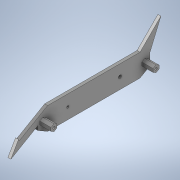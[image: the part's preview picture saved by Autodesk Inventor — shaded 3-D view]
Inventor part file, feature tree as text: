
AUTODESK INVENTOR PART (.ipt)
format: ipt  version: 2020 (Build 240168000, 168)  size: 182,272 bytes
history: native  units: in
note: dims shown in document units (in); Inventor stores cm internally (conversion verified against a paired STEP export)
features: other x3, extrude x2, sketch x2
ambient origin geometry x8: Origin, YZ Plane, XZ Plane, XY Plane, X Axis, Y Axis, Z Axis, Center Point
bodies: Solid1 (feature_tree)
feature tree (7):
  other  "HexWheelGuard.ipt"
  extrude  "Extrusion1"  TaperAngle=0.0deg  [1 undecoded]
  extrude  "Extrusion2"  Depth=0.5906in
  other  "Solid1::HexWheelGuard.ipt"
  other  "TaggingFeature1"
  sketch  "Sketch1"  dims[d0=0.3937in d6=0.0in d7=0.0in]
  sketch  "Sketch2"  dims[d9=0.315in d10=1.4843in d11=60.0deg d12=0.0787in d13=0.3937in d14=0.0in d20=0.3937in d21=0.5906in d22=1.1024in]
note: 1 required parameter value undecoded (feature->parameter linkage not recoverable at this tier; creation-order binding heuristic only, values carry confidence <= 0.55)
